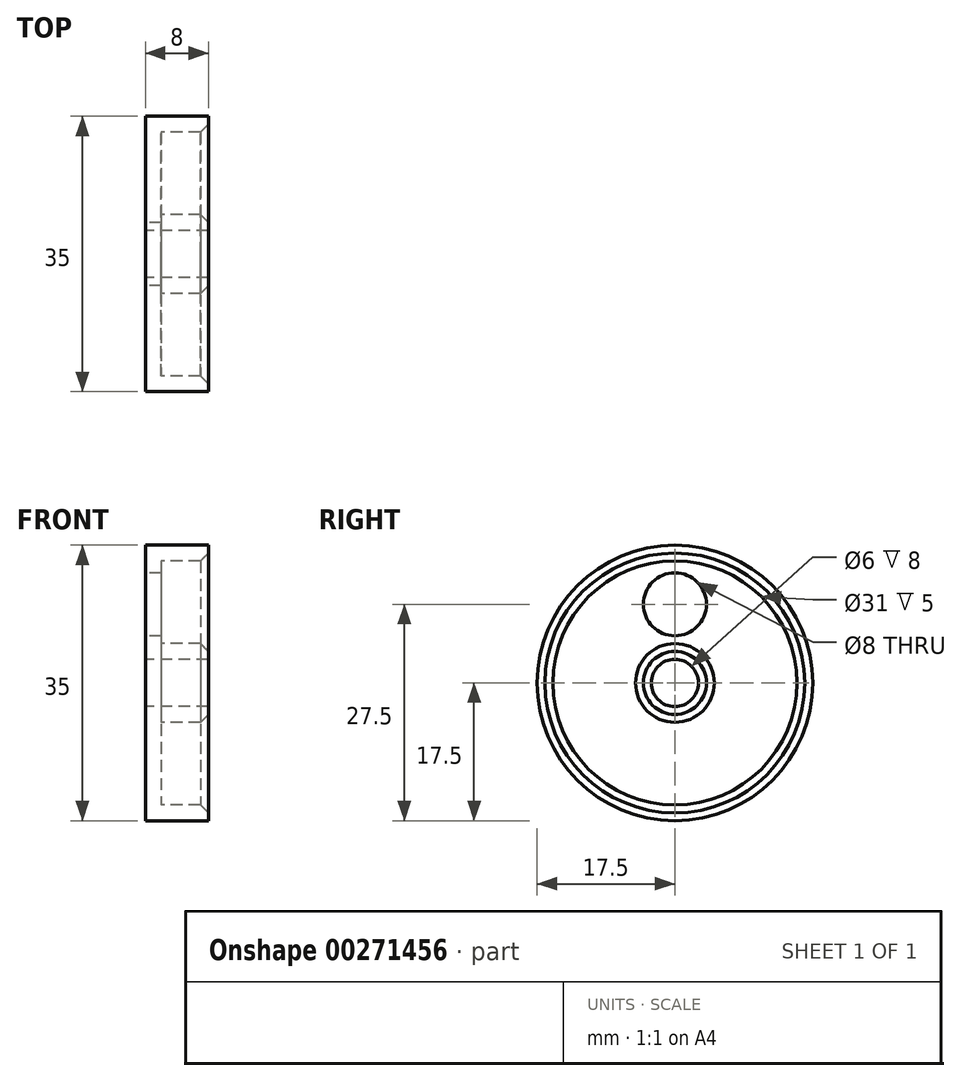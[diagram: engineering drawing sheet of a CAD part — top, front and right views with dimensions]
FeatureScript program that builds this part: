
annotation { "Feature Type Name" : "Feature", "Feature Type Description" : "" }
export const myFeature = defineFeature(function(context is Context, id is Id, definition is map)
    precondition{}
    {
        {
            var Q0;
            Q0=qCreatedBy(makeId("Top.planeOp"),FACE);
            var sketch = newSketch(context, id + "F0", { "sketchPlane" : qUnion([Q0])});
            skLineSegment(sketch, "E0.bottom", {"start": v(0, 0) * mm, "end": v(8, 0) * mm});
            skLineSegment(sketch, "E0.top", {"start": v(0, 17.5) * mm, "end": v(8, 17.5) * mm});
            skLineSegment(sketch, "E0.left", {"start": v(0, 0) * mm, "end": v(0, 17.5) * mm});
            skLineSegment(sketch, "E0.right", {"start": v(8, 0) * mm, "end": v(8, 17.5) * mm});
            skSolve(sketch);
        }
        {
            var Q0;
            Q0 = qSketchRegion(id + "F0", true);
            var Q1;
            Q1=sQuery(id+"F0.wireOp",EDGE,"E0.bottom");
            revolve(context, id + "F1", {"entities" : qUnion([Q0]), "axis" : qUnion([Q1]), "revolveType" : RevolveType.FULL});
        }
        {
            var Q0;
            Q0=qCreatedBy(makeId("Right.planeOp"),FACE);
            var sketch = newSketch(context, id + "F2", { "sketchPlane" : qUnion([Q0])});
            skPoint(sketch, "E1", {"position": v(0, 0) * mm});
            skSolve(sketch);
        }
        {
            var Q0;
            Q0=sQuery(id+"F2.wireOp",VERTEX,"E1");
            var Q1;
            Q1=makeQuery(id+"F1.opRevolve","SWEPT_BODY",BODY,{"disambiguationData":[OSD([sQuery(id+"F0.wireOp",EDGE,"E0.bottom"),sQuery(id+"F0.wireOp",EDGE,"E0.top"),sQuery(id+"F0.wireOp",EDGE,"E0.left"),sQuery(id+"F0.wireOp",EDGE,"E0.right")])]});
            hole(context, id + "F3", {"style" : HoleStyle.SIMPLE, "endStyle" : HoleEndStyle.THROUGH, "oppositeDirection" : true, "holeDiameter" : 6 * mm, "tappedDepth" : 12 * mm, "tapClearance" : 3, "locations" : qUnion([Q0]), "scope" : qUnion([Q1])});
        }
        {
            var Q0;
            Q0=makeQuery(id+"F1.opRevolve","SWEPT_FACE",FACE,{"disambiguationData":[OSD([sQuery(id+"F0.wireOp",EDGE,"E0.right")])]});
            shell(context, id + "F4", {"entities" : qUnion([Q0]), "thickness" : 2 * mm});
        }
        {
            var Q0;
            Q0=qCreatedBy(makeId("Right.planeOp"),FACE);
            var sketch = newSketch(context, id + "F5", { "sketchPlane" : qUnion([Q0])});
            skPoint(sketch, "E2", {"position": v(0, 0) * mm});
            skPoint(sketch, "E3", {"position": v(0, 10) * mm});
            skSolve(sketch);
        }
        {
            var Q0;
            Q0=sQuery(id+"F5.wireOp",VERTEX,"E3");
            var Q1;
            Q1=makeQuery(id+"F1.opRevolve","SWEPT_BODY",BODY,{"disambiguationData":[OSD([sQuery(id+"F0.wireOp",EDGE,"E0.bottom"),sQuery(id+"F0.wireOp",EDGE,"E0.top"),sQuery(id+"F0.wireOp",EDGE,"E0.left"),sQuery(id+"F0.wireOp",EDGE,"E0.right")])]});
            hole(context, id + "F6", {"style" : HoleStyle.SIMPLE, "endStyle" : HoleEndStyle.THROUGH, "oppositeDirection" : true, "holeDiameter" : 8 * mm, "tappedDepth" : 12 * mm, "tapClearance" : 3, "locations" : qUnion([Q0]), "scope" : qUnion([Q1])});
        }
        {
            var Q0;
            Q0=makeQuery(id+"F4.opShell","OFFSET_EDGE",EDGE,{"disambiguationData":[OSD([sQuery(id+"F0.wireOp",EDGE,"E0.right"),sQuery(id+"F3.hole-0.sketch.wireOp",EDGE,"core_line_2")])]});
            chamfer(context, id + "F7", {"entities" : qUnion([Q0]), "width" : 1 * mm, "tangentPropagation" : true});
        }
    });
